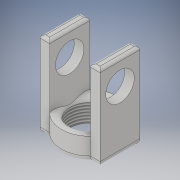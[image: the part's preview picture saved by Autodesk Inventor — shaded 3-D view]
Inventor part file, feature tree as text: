
AUTODESK INVENTOR PART (.ipt)
format: ipt  version: 2019 (Build 230136000, 136)  size: 194,560 bytes
history: native  units: mm
features: extrude x3, sketch x3, fillet x2, thread x1
ambient origin geometry x8: Origin, YZ Plane, XZ Plane, XY Plane, X Axis, Y Axis, Z Axis, Center Point
bodies: Solid1 (feature_tree)
feature tree (9):
  extrude  "Extrusion1"  Depth=10.0mm
  extrude  "Extrusion2"  Depth=10.0mm TaperAngle=0.0deg
  extrude  "Extrusion3"  Depth=10.0mm TaperAngle=0.0deg
  fillet  "Fillet1"  Radius=0.5mm
  fillet  "Fillet2"  Radius=1.0mm
  thread  "Thread1"  [1 undecoded]
  sketch  "Sketch1"  dims[d0=7.0mm d1=10.0mm]
  sketch  "Sketch2"  dims[d2=5.0mm d3=0.0mm d4=10.0mm d5=0.0mm]
  sketch  "Sketch3"  dims[d6=5.0mm d7=14.0mm d8=0.0mm d9=0.5mm d10=1.0mm d11=10.0mm d12=0.0mm]
note: 1 required parameter value undecoded (feature->parameter linkage not recoverable at this tier; creation-order binding heuristic only, values carry confidence <= 0.55)
